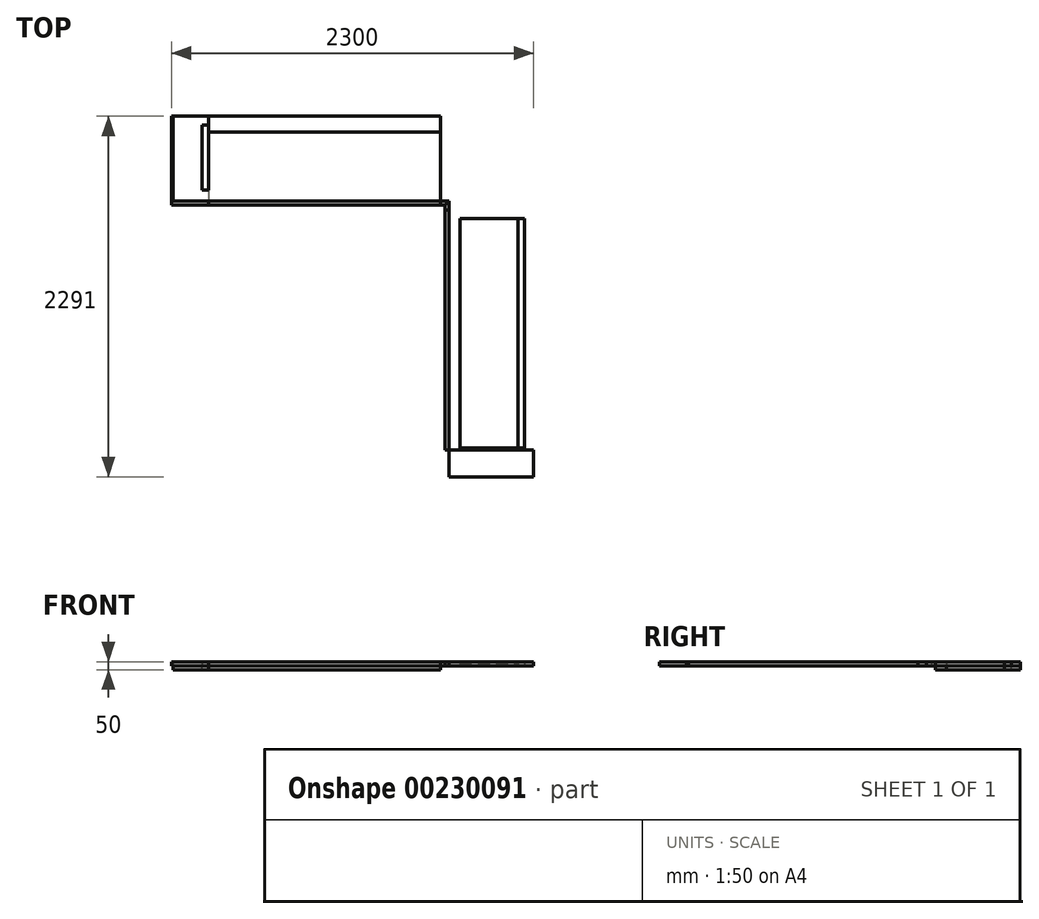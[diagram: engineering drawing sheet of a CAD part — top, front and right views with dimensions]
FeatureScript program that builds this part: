
annotation { "Feature Type Name" : "Feature", "Feature Type Description" : "" }
export const myFeature = defineFeature(function(context is Context, id is Id, definition is map)
    precondition{}
    {
        {
            var Q0;
            Q0=qCreatedBy(makeId("Top.planeOp"),FACE);
            var sketch = newSketch(context, id + "F0", { "sketchPlane" : qUnion([Q0])});
            skLineSegment(sketch, "E0.bottom", {"start": v(-2290, 0) * mm, "end": v(0, 0) * mm});
            skLineSegment(sketch, "E0.top", {"start": v(-2290, -538) * mm, "end": v(-538, -538) * mm});
            skLineSegment(sketch, "E0.left", {"start": v(-2290, 0) * mm, "end": v(-2290, -538) * mm});
            skLineSegment(sketch, "E1.top", {"start": v(-538, -2291) * mm, "end": v(0, -2291) * mm});
            skLineSegment(sketch, "E1.left", {"start": v(-538, -538) * mm, "end": v(-538, -2291) * mm});
            skLineSegment(sketch, "E1.right", {"start": v(0, 0) * mm, "end": v(0, -2291) * mm});
            skLineSegment(sketch, "E2.right", {"start": v(538, 536.14) * mm, "end": v(538, 536.14) * mm});
            skLineSegment(sketch, "E3.bottom", {"start": v(-518, -453) * mm, "end": v(-453, -453) * mm});
            skLineSegment(sketch, "E3.top", {"start": v(-518, -518) * mm, "end": v(-453, -518) * mm});
            skLineSegment(sketch, "E3.left", {"start": v(-518, -518) * mm, "end": v(-518, -453) * mm});
            skLineSegment(sketch, "E3.right", {"start": v(-453, -518) * mm, "end": v(-453, -453) * mm});
            skLineSegment(sketch, "E4.bottom", {"start": v(-468, -649.14) * mm, "end": v(-58, -649.14) * mm});
            skLineSegment(sketch, "E4.top", {"start": v(-468, -2106.14) * mm, "end": v(-58, -2106.14) * mm});
            skLineSegment(sketch, "E4.left", {"start": v(-468, -649.14) * mm, "end": v(-468, -2106.14) * mm});
            skLineSegment(sketch, "E4.right", {"start": v(-58, -649.14) * mm, "end": v(-58, -2106.14) * mm});
            skLineSegment(sketch, "E5.bottom", {"start": v(-2106.16, -56) * mm, "end": v(-706.16, -56) * mm});
            skLineSegment(sketch, "E5.top", {"start": v(-2106.16, -468) * mm, "end": v(-706.16, -468) * mm});
            skLineSegment(sketch, "E5.left", {"start": v(-2106.16, -56) * mm, "end": v(-2106.16, -468) * mm});
            skLineSegment(sketch, "E5.right", {"start": v(-706.16, -56) * mm, "end": v(-706.16, -468) * mm});
            skLineSegment(sketch, "E6", {"start": v(-100, -2291) * mm, "end": v(-100, -649.14) * mm, "construction": true});
            skLineSegment(sketch, "E7", {"start": v(-2106.16, -100) * mm, "end": v(-706.16, -100) * mm, "construction": true});
            skPoint(sketch, "E8.orphan", {"position": v(-2290, -100) * mm});
            skPoint(sketch, "E9.orphan", {"position": v(-100, -2291) * mm});
            skSolve(sketch);
        }
        {
            var Q0;
            Q0=makeQuery(id+"F0.imprint","IMPRINT",FACE,{"disambiguationData":[TD([[makeQuery(id+"F0.imprint","IMPRINT",EDGE,{"derivedFrom":sQuery(id+"F0.wireOp",EDGE,"E0.bottom")}),-1.0]])]});
            var sketch = newSketch(context, id + "F1", { "sketchPlane" : qUnion([Q0])});
            skLineSegment(sketch, "E10.bottom", {"start": v(2035.4, 100) * mm, "end": v(3235.4, 100) * mm});
            skLineSegment(sketch, "E11", {"start": v(3235.4, 100) * mm, "end": v(3235.4, -2300) * mm});
            skLineSegment(sketch, "E12", {"start": v(2035.4, 100) * mm, "end": v(2035.4, -2300) * mm});
            skLineSegment(sketch, "E13.0", {"start": v(-2300, 0) * mm, "end": v(0, 0) * mm});
            skLineSegment(sketch, "E14.0", {"start": v(-2300, -538) * mm, "end": v(-538, -538) * mm});
            skLineSegment(sketch, "E15.0", {"start": v(-2300, 0) * mm, "end": v(-2300, -538) * mm});
            skLineSegment(sketch, "E16.0", {"start": v(0, 0) * mm, "end": v(0, -2300) * mm});
            skLineSegment(sketch, "E17.0", {"start": v(-563, -2300) * mm, "end": v(0, -2300) * mm});
            skLineSegment(sketch, "E18.0", {"start": v(-538, -538) * mm, "end": v(-538, -2300) * mm});
            skLineSegment(sketch, "E19.0", {"start": v(-563, -595) * mm, "end": v(0, -595) * mm});
            skLineSegment(sketch, "E20.0", {"start": v(-563, -2120) * mm, "end": v(0, -2120) * mm});
            skLineSegment(sketch, "E21.0", {"start": v(-590, 0) * mm, "end": v(-590, -563) * mm});
            skLineSegment(sketch, "E22.0", {"start": v(-518, -453) * mm, "end": v(-453, -453) * mm});
            skLineSegment(sketch, "E23.0", {"start": v(-518, -518) * mm, "end": v(-518, -453) * mm});
            skLineSegment(sketch, "E24.0", {"start": v(-518, -518) * mm, "end": v(-453, -518) * mm});
            skLineSegment(sketch, "E25.0", {"start": v(-453, -518) * mm, "end": v(-453, -453) * mm});
            skLineSegment(sketch, "E26", {"start": v(-538, -538) * mm, "end": v(-518, -518) * mm});
            skLineSegment(sketch, "E27", {"start": v(-453, -453) * mm, "end": v(0, 0) * mm});
            skLineSegment(sketch, "E28.0", {"start": v(-563, -563) * mm, "end": v(-563, -2300) * mm});
            skLineSegment(sketch, "E28.1", {"start": v(-2300, -563) * mm, "end": v(-563, -563) * mm});
            skLineSegment(sketch, "E29", {"start": v(-2300, -563) * mm, "end": v(-2300, -538) * mm});
            skLineSegment(sketch, "E30", {"start": v(-563, -563) * mm, "end": v(-538, -538) * mm});
            skPoint(sketch, "E31.orphan", {"position": v(-538, -2300) * mm});
            skLineSegment(sketch, "E32", {"start": v(-100, -595) * mm, "end": v(-100, -2120) * mm});
            skLineSegment(sketch, "E33", {"start": v(-590, -100) * mm, "end": v(-2065, -100) * mm});
            skLineSegment(sketch, "E34.bottom", {"start": v(-100, -595) * mm, "end": v(0, -595) * mm});
            skLineSegment(sketch, "E34.top", {"start": v(-100, -2120) * mm, "end": v(0, -2120) * mm});
            skLineSegment(sketch, "E34.right", {"start": v(0, -595) * mm, "end": v(0, -2120) * mm});
            skLineSegment(sketch, "E35.bottom", {"start": v(-100, -2120) * mm, "end": v(-538, -2120) * mm});
            skLineSegment(sketch, "E35.top", {"start": v(-100, -595) * mm, "end": v(-538, -595) * mm});
            skLineSegment(sketch, "E35.left", {"start": v(-100, -2120) * mm, "end": v(-100, -595) * mm});
            skLineSegment(sketch, "E35.right", {"start": v(-538, -2120) * mm, "end": v(-538, -595) * mm});
            skLineSegment(sketch, "E36", {"start": v(-2065, 0) * mm, "end": v(-2065, -563) * mm});
            skLineSegment(sketch, "E37", {"start": v(2035.4, -2300) * mm, "end": v(3235.4, -2300) * mm});
            skLineSegment(sketch, "E38.0", {"start": v(3235.4, 3) * mm, "end": v(3235.4, -2300) * mm});
            skLineSegment(sketch, "E39.0", {"start": v(2697.4, -2300) * mm, "end": v(3235.4, -2300) * mm});
            skLineSegment(sketch, "E40.0", {"start": v(2697.4, -535) * mm, "end": v(2697.4, -2300) * mm});
            skLineSegment(sketch, "E41.0", {"start": v(2697.4, -592) * mm, "end": v(3235.4, -592) * mm});
            skLineSegment(sketch, "E42.0", {"start": v(2697.4, -2120) * mm, "end": v(3235.4, -2120) * mm});
            skLineSegment(sketch, "E43.0", {"start": v(2717.4, -515) * mm, "end": v(2782.4, -515) * mm});
            skLineSegment(sketch, "E44.0", {"start": v(2782.4, -515) * mm, "end": v(2782.4, -450) * mm});
            skLineSegment(sketch, "E45", {"start": v(2697.4, -535) * mm, "end": v(2717.4, -515) * mm});
            skLineSegment(sketch, "E46", {"start": v(2782.4, -450) * mm, "end": v(3235.4, 3) * mm});
            skLineSegment(sketch, "E47", {"start": v(3135.4, -592) * mm, "end": v(3135.4, -2120) * mm});
            skLineSegment(sketch, "E48.bottom", {"start": v(3135.4, -592) * mm, "end": v(3235.4, -592) * mm});
            skLineSegment(sketch, "E48.top", {"start": v(3135.4, -2120) * mm, "end": v(3235.4, -2120) * mm});
            skLineSegment(sketch, "E48.right", {"start": v(3235.4, -592) * mm, "end": v(3235.4, -2120) * mm});
            skLineSegment(sketch, "E49.bottom", {"start": v(3135.4, -2120) * mm, "end": v(2697.4, -2120) * mm});
            skLineSegment(sketch, "E49.top", {"start": v(3135.4, -592) * mm, "end": v(2697.4, -592) * mm});
            skLineSegment(sketch, "E49.left", {"start": v(3135.4, -2120) * mm, "end": v(3135.4, -592) * mm});
            skLineSegment(sketch, "E49.right", {"start": v(2697.4, -2120) * mm, "end": v(2697.4, -592) * mm});
            skLineSegment(sketch, "E50.0", {"start": v(2035.4, -2300) * mm, "end": v(2035.4, 0) * mm});
            skLineSegment(sketch, "E51.0", {"start": v(2573.4, -2297) * mm, "end": v(2573.4, -535) * mm});
            skLineSegment(sketch, "E52.0", {"start": v(2035.4, -2300) * mm, "end": v(2573.4, -2300) * mm});
            skLineSegment(sketch, "E53.0", {"start": v(2488.4, -518) * mm, "end": v(2488.4, -453) * mm});
            skLineSegment(sketch, "E54.0", {"start": v(2553.4, -515) * mm, "end": v(2488.4, -515) * mm});
            skLineSegment(sketch, "E55", {"start": v(2573.4, -535) * mm, "end": v(2553.4, -515) * mm});
            skLineSegment(sketch, "E56", {"start": v(2488.4, -453) * mm, "end": v(2035.4, 0) * mm});
            skLineSegment(sketch, "E57", {"start": v(2135.4, -587) * mm, "end": v(2135.4, -2065) * mm});
            skLineSegment(sketch, "E58", {"start": v(2035.4, -587) * mm, "end": v(2573.4, -587) * mm});
            skLineSegment(sketch, "E59", {"start": v(2035.4, -2065) * mm, "end": v(2573.4, -2065) * mm});
            skSolve(sketch);
        }
        {
            var Q0;
            {var subQ0=sQuery(id+"F1.wireOp",EDGE,"E15.0");Q0=makeQuery(id+"F1.imprint","IMPRINT",FACE,{"disambiguationData":[TD([[makeQuery(id+"F1.imprint","IMPRINT",EDGE,{"derivedFrom":subQ0}),1.0]])]});}
            var Q1;
            Q1=makeQuery(id+"F1.imprint","IMPRINT",FACE,{"disambiguationData":[TD([[makeQuery(id+"F1.imprint","IMPRINT",EDGE,{"derivedFrom":sQuery(id+"F1.wireOp",EDGE,"E22.0")}),1.0]])]});
            var Q2;
            {var subQ5=makeQuery(id+"F0.imprint","IMPRINT",EDGE,{"derivedFrom":sQuery(id+"F0.wireOp",EDGE,"E4.left")});Q2=makeQuery(id+"F1.imprint","IMPRINT",FACE,{"disambiguationData":[TD([[makeQuery(id+"F1.imprint","IMPRINT",EDGE,{"derivedFrom":subQ5}),1.0]])]});}
            var Q3;
            {var subQ4=sQuery(id+"F1.wireOp",EDGE,"E35.bottom");Q3=makeQuery(id+"F1.imprint","IMPRINT",FACE,{"disambiguationData":[TD([[makeQuery(id+"F1.imprint","IMPRINT",EDGE,{"derivedFrom":subQ4}),1.0]])]});}
            extrude(context, id + "F2", {"entities" : qUnion([Q0, Q1, Q2, Q3]), "depth" : 17 * mm});
        }
        {
            var Q0;
            {var subQ7=makeQuery(id+"F0.imprint","IMPRINT",EDGE,{"derivedFrom":sQuery(id+"F0.wireOp",EDGE,"E5.bottom")});Q0=makeQuery(id+"F1.imprint","IMPRINT",FACE,{"disambiguationData":[TD([[makeQuery(id+"F1.imprint","IMPRINT",EDGE,{"derivedFrom":subQ7}),1.0]])]});}
            var Q1;
            {var subQ5=makeQuery(id+"F0.imprint","IMPRINT",EDGE,{"derivedFrom":sQuery(id+"F0.wireOp",EDGE,"E5.bottom")});Q1=makeQuery(id+"F1.imprint","IMPRINT",FACE,{"disambiguationData":[TD([[makeQuery(id+"F1.imprint","IMPRINT",EDGE,{"derivedFrom":subQ5}),-1.0]])]});}
            var Q2;
            Q2=makeQuery(id+"F1.imprint","IMPRINT",FACE,{"disambiguationData":[TD([[makeQuery(id+"F1.imprint","IMPRINT",EDGE,{"derivedFrom":sQuery(id+"F1.wireOp",EDGE,"E24.0")}),-1.0]])]});
            var Q3;
            {var subQ0=sQuery(id+"F1.wireOp",EDGE,"E34.top");Q3=makeQuery(id+"F1.imprint","IMPRINT",FACE,{"disambiguationData":[TD([[makeQuery(id+"F1.imprint","IMPRINT",EDGE,{"derivedFrom":subQ0}),-1.0]])]});}
            extrude(context, id + "F3", {"entities" : qUnion([Q0, Q1, Q2, Q3]), "oppositeDirection" : true, "depth" : 25 * mm});
        }
        {
            var Q0;
            {var subQ5=makeQuery(id+"F0.imprint","IMPRINT",EDGE,{"derivedFrom":sQuery(id+"F0.wireOp",EDGE,"E5.top")});Q0=makeQuery(id+"F1.imprint","IMPRINT",FACE,{"disambiguationData":[TD([[makeQuery(id+"F1.imprint","IMPRINT",EDGE,{"derivedFrom":subQ5}),1.0]])]});}
            var Q1;
            {var subQ12=makeQuery(id+"F0.imprint","IMPRINT",EDGE,{"derivedFrom":sQuery(id+"F0.wireOp",EDGE,"E5.top")});Q1=makeQuery(id+"F1.imprint","IMPRINT",FACE,{"disambiguationData":[TD([[makeQuery(id+"F1.imprint","IMPRINT",EDGE,{"derivedFrom":subQ12}),-1.0]])]});}
            var Q2;
            {var subQ5=makeQuery(id+"F0.imprint","IMPRINT",EDGE,{"derivedFrom":sQuery(id+"F0.wireOp",EDGE,"E4.right")});Q2=makeQuery(id+"F1.imprint","IMPRINT",FACE,{"disambiguationData":[TD([[makeQuery(id+"F1.imprint","IMPRINT",EDGE,{"derivedFrom":subQ5}),-1.0]])]});}
            var Q3;
            {var subQ5=sQuery(id+"F1.wireOp",EDGE,"E34.bottom");Q3=makeQuery(id+"F1.imprint","IMPRINT",FACE,{"disambiguationData":[TD([[makeQuery(id+"F1.imprint","IMPRINT",EDGE,{"derivedFrom":subQ5}),-1.0]])]});}
            extrude(context, id + "F4", {"entities" : qUnion([Q0, Q1, Q2, Q3]), "depth" : 25 * mm});
        }
        {
            var Q0;
            {var subQ0=sQuery(id+"F1.wireOp",EDGE,"E29");Q0=makeQuery(id+"F1.imprint","IMPRINT",FACE,{"disambiguationData":[TD([[makeQuery(id+"F1.imprint","IMPRINT",EDGE,{"derivedFrom":subQ0}),-1.0]])]});}
            var Q1;
            {var subQ0=sQuery(id+"F1.wireOp",EDGE,"E30");Q1=makeQuery(id+"F1.imprint","IMPRINT",FACE,{"disambiguationData":[TD([[makeQuery(id+"F1.imprint","IMPRINT",EDGE,{"derivedFrom":subQ0}),1.0]])]});}
            var Q2;
            {var subQ0=sQuery(id+"F1.wireOp",EDGE,"E19.0");Q2=makeQuery(id+"F1.imprint","IMPRINT",FACE,{"disambiguationData":[TD([[makeQuery(id+"F1.imprint","IMPRINT",EDGE,{"derivedFrom":subQ0}),-1.0]])]});}
            extrude(context, id + "F5", {"entities" : qUnion([Q0, Q1, Q2]), "depth" : 25 * mm});
        }
        {
            var Q0;
            {var subQ0=sQuery(id+"F1.wireOp",EDGE,"ff1c606a-3cd1-44da-8a54-acbadf63f554.0");var subQ1=sQuery(id+"F1.wireOp",EDGE,"E14.0");var subQ2=makeQuery(id+"F1.imprint","INTERSECT",VERTEX,{"derivedFrom":[subQ1,subQ0]});Q0=makeQuery(id+"F1.imprint","IMPRINT",FACE,{"disambiguationData":[TD([[makeQuery(id+"F1.imprint","IMPRINT",EDGE,{"disambiguationData":[TD([[subQ2,-1.0]])],"derivedFrom":subQ1}),-1.0]])]});}
            var Q1;
            {var subQ2=sQuery(id+"F1.wireOp",EDGE,"E19.0");Q1=makeQuery(id+"F1.imprint","IMPRINT",FACE,{"disambiguationData":[TD([[makeQuery(id+"F1.imprint","IMPRINT",EDGE,{"derivedFrom":subQ2}),1.0]])]});}
            var Q2;
            {var subQ5=sQuery(id+"F1.wireOp",EDGE,"E20.0");Q2=makeQuery(id+"F1.imprint","IMPRINT",FACE,{"disambiguationData":[TD([[makeQuery(id+"F1.imprint","IMPRINT",EDGE,{"derivedFrom":subQ5}),-1.0]])]});}
            extrude(context, id + "F6", {"entities" : qUnion([Q0, Q1, Q2]), "depth" : 25 * mm});
        }
    });
